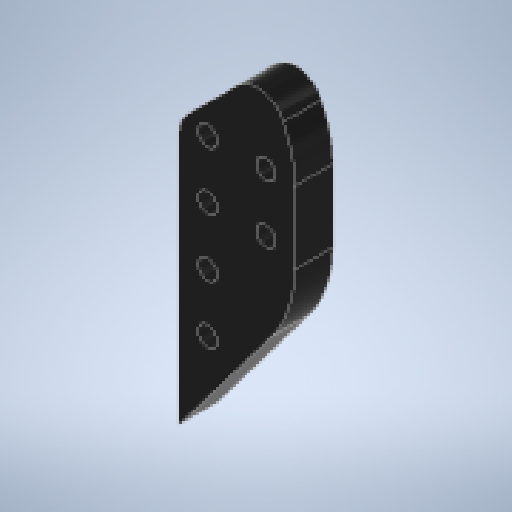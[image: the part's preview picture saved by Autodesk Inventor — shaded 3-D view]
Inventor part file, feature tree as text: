
AUTODESK INVENTOR PART (.ipt)
format: ipt  version: 2023 (Build 270158000, 158)  size: 162,816 bytes
history: native  units: in
note: dims shown in document units (in); Inventor stores cm internally (conversion verified against a paired STEP export)
features: other x3, sketch x1, plane x1, extrude x1, fillet x1, reference x1
ambient origin geometry x8: Origin, YZ Plane, XZ Plane, XY Plane, X Axis, Y Axis, Z Axis, Center Point
bodies: Solid1 (feature_tree)
feature tree (8):
  sketch  "Sketch1"  dims[d0=1.0in d1=0.0in d2=0.125in]
  plane  "Work Plane1"
  extrude  "Extrusion1"  Depth=0.125in
  fillet  "Fillet1"  [1 undecoded]
  reference  "Reference1"
  other  "<userpath> Hah\Documents\GitHub\spin-up-cad\spin-up-18_1\MainAssy.iam"
  other  "MainAssy.iam"
  other  "IntakeAftArm:2"
note: 1 required parameter value undecoded (feature->parameter linkage not recoverable at this tier; creation-order binding heuristic only, values carry confidence <= 0.55)
